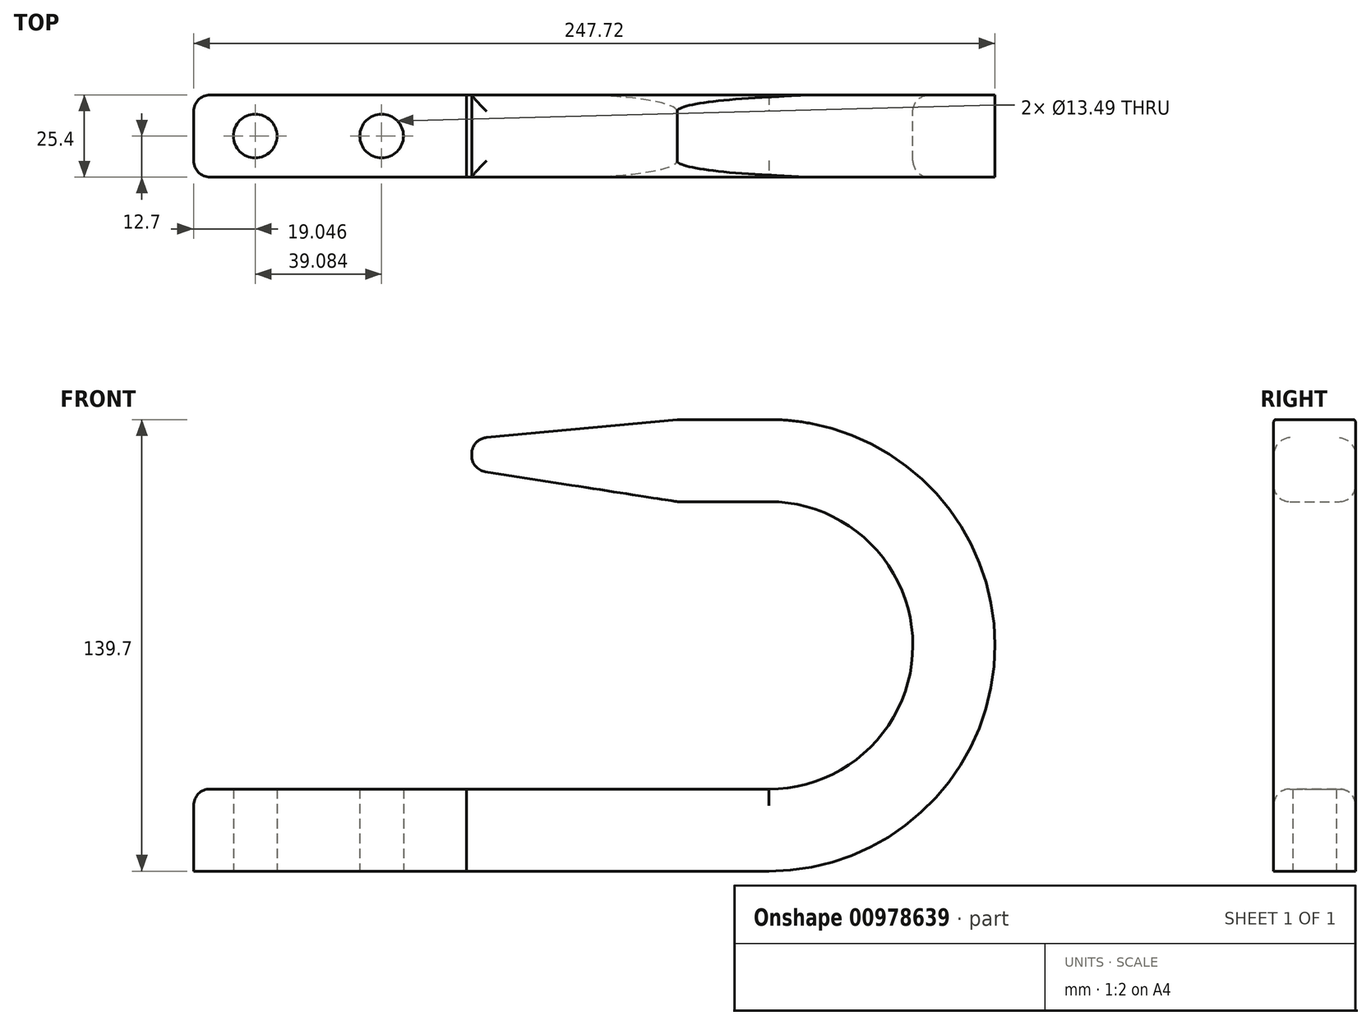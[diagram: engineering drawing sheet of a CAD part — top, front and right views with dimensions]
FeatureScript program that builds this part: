
annotation { "Feature Type Name" : "Feature", "Feature Type Description" : "" }
export const myFeature = defineFeature(function(context is Context, id is Id, definition is map)
    precondition{}
    {
        {
            var Q0;
            Q0=qCreatedBy(makeId("Top.planeOp"),FACE);
            cPlane(context, id + "F0", {"entities" : qUnion([Q0]), "cplaneType" : CPlaneType.OFFSET, "offset" : 12.7 * mm, "width" : 152.4 * mm, "height" : 152.4 * mm});
        }
        {
            var Q0;
            Q0=qCreatedBy(makeId("Front.planeOp"),FACE);
            var sketch = newSketch(context, id + "F1", { "sketchPlane" : qUnion([Q0])});
            skLineSegment(sketch, "E0.bottom", {"start": v(-22.33, -12.7) * mm, "end": v(62, -12.7) * mm});
            skLineSegment(sketch, "E0.top", {"start": v(-22.33, 12.7) * mm, "end": v(62, 12.7) * mm});
            skLineSegment(sketch, "E0.left", {"start": v(-22.33, -12.7) * mm, "end": v(-22.33, 12.7) * mm});
            skLineSegment(sketch, "E0.right", {"start": v(62, -12.7) * mm, "end": v(62, 12.7) * mm});
            skPoint(sketch, "E0.middle", {"position": v(19.83, 0) * mm});
            skLineSegment(sketch, "E1.bottom", {"start": v(62, -12.7) * mm, "end": v(155.47, -12.7) * mm});
            skLineSegment(sketch, "E1.top", {"start": v(62, 12.7) * mm, "end": v(155.47, 12.7) * mm});
            skLineSegment(sketch, "E1.right", {"start": v(155.47, -12.7) * mm, "end": v(155.47, 12.7) * mm});
            skPoint(sketch, "E1.middle", {"position": v(108.73, 0) * mm});
            skLineSegment(sketch, "E2.bottom", {"start": v(155.54, 101.6) * mm, "end": v(127.12, 101.6) * mm});
            skLineSegment(sketch, "E2.top", {"start": v(155.54, 127) * mm, "end": v(127.12, 127) * mm});
            skLineSegment(sketch, "E2.left", {"start": v(155.54, 101.6) * mm, "end": v(155.54, 127) * mm});
            skLineSegment(sketch, "E3", {"start": v(127.12, 101.6) * mm, "end": v(127.12, 127) * mm});
            skLineSegment(sketch, "E4", {"start": v(127.12, 127) * mm, "end": v(63.62, 121.02) * mm});
            skLineSegment(sketch, "E5", {"start": v(63.62, 121.02) * mm, "end": v(63.62, 111.5) * mm});
            skLineSegment(sketch, "E6", {"start": v(63.62, 111.5) * mm, "end": v(127.12, 101.6) * mm});
            skArc(sketch, "E7", {"start": v(155.54, 101.6) * mm, "mid": v(199.99, 57.12) * mm, "end": v(155.47, 12.7) * mm});
            skArc(sketch, "E8", {"start": v(155.54, 127) * mm, "mid": v(225.39, 57.12) * mm, "end": v(155.47, -12.7) * mm});
            skSolve(sketch);
        }
        {
            var Q0;
            Q0=qCreatedBy(id+"F0.planeOp",FACE);
            var sketch = newSketch(context, id + "F2", { "sketchPlane" : qUnion([Q0])});
            skCircle(sketch, "E9", {"center": v(-3.28, 0) * mm, "radius": 6.75 * mm});
            skCircle(sketch, "E10", {"center": v(35.8, 0) * mm, "radius": 6.75 * mm});
            skSolve(sketch);
        }
        {
            var Q0;
            Q0=makeQuery(id+"F1.imprint","IMPRINT",FACE,{"disambiguationData":[TD([[makeQuery(id+"F1.imprint","IMPRINT",EDGE,{"derivedFrom":sQuery(id+"F1.wireOp",EDGE,"E0.bottom")}),1.0]])]});
            extrude(context, id + "F3", {"entities" : qUnion([Q0]), "depth" : 25.4 * mm, "offsetDistance" : 25.4 * mm, "symmetric" : true});
        }
        {
            var Q0;
            Q0=sQuery(id+"F2.wireOp",VERTEX,"E9.center");
            var Q1;
            Q1=sQuery(id+"F2.wireOp",VERTEX,"E10.center");
            var Q2;
            Q2=makeQuery(id+"F3.opExtrude","SWEPT_BODY",BODY,{"disambiguationData":[OSD([sQuery(id+"F1.wireOp",EDGE,"E0.bottom"),sQuery(id+"F1.wireOp",EDGE,"E0.top"),sQuery(id+"F1.wireOp",EDGE,"E0.left"),sQuery(id+"F1.wireOp",EDGE,"E0.right")])]});
            hole(context, id + "F4", {"style" : HoleStyle.SIMPLE, "endStyle" : HoleEndStyle.BLIND, "holeDiameter" : 13.5 * mm, "majorDiameter" : 6.35 * mm, "holeDepth" : 25.4 * mm, "isTappedThrough" : true, "tappedDepth" : 12.7 * mm, "tapClearance" : 3, "locations" : qUnion([Q0, Q1]), "scope" : qUnion([Q2])});
        }
        {
            var Q0;
            Q0=makeQuery(id+"F3.opExtrude","CAP_EDGE",EDGE,{"disambiguationData":[OSD([sQuery(id+"F1.wireOp",EDGE,"E0.top")])],"isStart":false});
            var Q1;
            Q1=makeQuery(id+"F3.opExtrude","CAP_EDGE",EDGE,{"disambiguationData":[OSD([sQuery(id+"F1.wireOp",EDGE,"E0.top")])],"isStart":true});
            var Q2;
            Q2=makeQuery(id+"F3.opExtrude","SWEPT_EDGE",EDGE,{"disambiguationData":[OSD([sQuery(id+"F1.wireOp",EDGE,"E0.top"),sQuery(id+"F1.wireOp",EDGE,"E0.left")])]});
            var Q3;
            Q3=makeQuery(id+"F3.opExtrude","CAP_EDGE",EDGE,{"disambiguationData":[OSD([sQuery(id+"F1.wireOp",EDGE,"E0.left")])],"isStart":true});
            var Q4;
            Q4=makeQuery(id+"F3.opExtrude","CAP_EDGE",EDGE,{"disambiguationData":[OSD([sQuery(id+"F1.wireOp",EDGE,"E0.left")])],"isStart":false});
            fillet(context, id + "F5", {"entities" : qUnion([Q0, Q1, Q2, Q3, Q4]), "radius" : 5.08 * mm, "tangentPropagation" : true, "allowEdgeOverflow" : false});
        }
        {
            var Q0;
            Q0=makeQuery(id+"F1.imprint","IMPRINT",FACE,{"disambiguationData":[TD([[makeQuery(id+"F1.imprint","IMPRINT",EDGE,{"derivedFrom":sQuery(id+"F1.wireOp",EDGE,"E1.bottom")}),1.0]])]});
            var Q1;
            Q1=makeQuery(id+"F1.imprint","IMPRINT",FACE,{"disambiguationData":[TD([[makeQuery(id+"F1.imprint","IMPRINT",EDGE,{"derivedFrom":sQuery(id+"F1.wireOp",EDGE,"E1.right")}),-1.0]])]});
            var Q2;
            Q2=makeQuery(id+"F1.imprint","IMPRINT",FACE,{"disambiguationData":[TD([[makeQuery(id+"F1.imprint","IMPRINT",EDGE,{"derivedFrom":sQuery(id+"F1.wireOp",EDGE,"E2.bottom")}),-1.0]])]});
            extrude(context, id + "F6", {"entities" : qUnion([Q0, Q1, Q2]), "depth" : 25.4 * mm, "offsetDistance" : 25.4 * mm, "symmetric" : true});
        }
        {
            var Q0;
            Q0=makeQuery(id+"F1.imprint","IMPRINT",FACE,{"disambiguationData":[TD([[makeQuery(id+"F1.imprint","IMPRINT",EDGE,{"derivedFrom":sQuery(id+"F1.wireOp",EDGE,"E3")}),1.0]])]});
            extrude(context, id + "F7", {"entities" : qUnion([Q0]), "operationType" : NewBodyOperationType.ADD, "depth" : 25.4 * mm, "offsetDistance" : 25.4 * mm, "symmetric" : true});
        }
        {
            var Q0;
            Q0=makeQuery(id+"F7.opExtrude","CAP_EDGE",EDGE,{"disambiguationData":[OSD([sQuery(id+"F1.wireOp",EDGE,"E4")])],"isStart":false});
            var Q1;
            Q1=makeQuery(id+"F7.opExtrude","CAP_EDGE",EDGE,{"disambiguationData":[OSD([sQuery(id+"F1.wireOp",EDGE,"E4")])],"isStart":true});
            var Q2;
            Q2=makeQuery(id+"F7.opExtrude","SWEPT_EDGE",EDGE,{"disambiguationData":[OSD([sQuery(id+"F1.wireOp",EDGE,"E4"),sQuery(id+"F1.wireOp",EDGE,"E5")])]});
            var Q3;
            Q3=makeQuery(id+"F6.opExtrude","CAP_EDGE",EDGE,{"disambiguationData":[OSD([sQuery(id+"F1.wireOp",EDGE,"ef8acae8-52aa-4b2f-847a-466628e56280")])],"isStart":true});
            var Q4;
            Q4=makeQuery(id+"F6.opExtrude","CAP_EDGE",EDGE,{"disambiguationData":[OSD([sQuery(id+"F1.wireOp",EDGE,"ef8acae8-52aa-4b2f-847a-466628e56280")])],"isStart":false});
            var Q5;
            Q5=makeQuery(id+"F7.opExtrude","SWEPT_EDGE",EDGE,{"disambiguationData":[OSD([sQuery(id+"F1.wireOp",EDGE,"E5"),sQuery(id+"F1.wireOp",EDGE,"E6")])]});
            var Q6;
            Q6=makeQuery(id+"F6.opExtrude","CAP_EDGE",EDGE,{"disambiguationData":[OSD([sQuery(id+"F1.wireOp",EDGE,"E1.top")])],"isStart":true});
            var Q7;
            Q7=makeQuery(id+"F6.opExtrude","CAP_EDGE",EDGE,{"disambiguationData":[OSD([sQuery(id+"F1.wireOp",EDGE,"E1.top")])],"isStart":false});
            fillet(context, id + "F8", {"entities" : qUnion([Q0, Q1, Q2, Q3, Q4, Q5, Q6, Q7]), "radius" : 5.08 * mm, "tangentPropagation" : true, "allowEdgeOverflow" : false});
        }
    });
